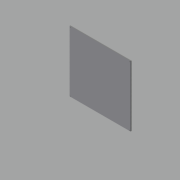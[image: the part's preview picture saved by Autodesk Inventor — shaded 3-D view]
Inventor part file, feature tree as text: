
AUTODESK INVENTOR PART (.ipt)
format: ipt  version: 2013 (Build 170138000, 138)  size: 385,024 bytes
history: native  units: mm
features: other x2, extrude x1, hole x1
ambient origin geometry x8: Origin, YZ Plane, XZ Plane, XY Plane, X Axis, Y Axis, Z Axis, Center Point
bodies: Solid1 (feature_tree)
feature tree (4):
  extrude  "Extrusion1"  Depth=214.0mm
  hole  "Hole1"  [1 undecoded]
  other  "Decal1"
  other  "Image1"
note: 1 required parameter value undecoded (feature->parameter linkage not recoverable at this tier; creation-order binding heuristic only, values carry confidence <= 0.55)
